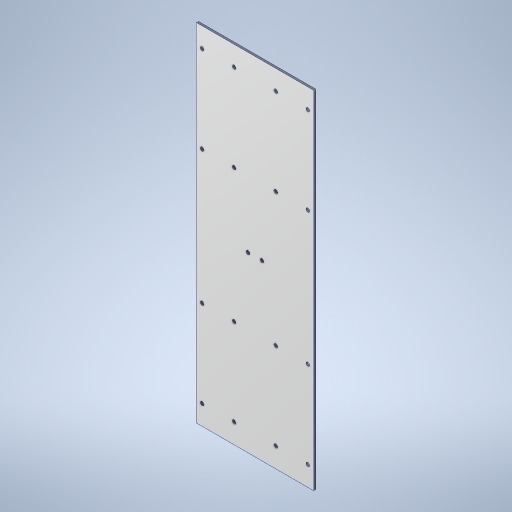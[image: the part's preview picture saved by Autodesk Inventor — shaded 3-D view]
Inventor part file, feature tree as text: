
AUTODESK INVENTOR PART (.ipt)
format: ipt  version: 2024 (Build 280153000, 153)  size: 334,848 bytes
history: native  units: mm
features: sketch x5, extrude x4, hole x3, other x2
ambient origin geometry x8: Origin, YZ Plane, XZ Plane, XY Plane, X Axis, Y Axis, Z Axis, Center Point
bodies: Body1 (feature_tree), Body2 (feature_tree)
feature tree (14):
  other  "Laminate"
  sketch  "Sketch1"  dims[d0=169.5mm d1=499.0mm]
  extrude  "Extrusion1"  Depth=499.0mm
  extrude  "Extrusion2"  Depth=2.9mm TaperAngle=0.0deg
  extrude  "Extrusion3"  Depth=250.0mm
  hole  "Hole2"  [1 undecoded]
  hole  "Hole3"  [1 undecoded]
  hole  "Hole1"  [1 undecoded]
  extrude  "Extrusion4"  TaperAngle=0.0deg  [1 undecoded]
  other  "Core"
  sketch  "Sketch2"  dims[d2=3.0mm d3=0.0mm d4=2.9mm d5=0.0mm]
  sketch  "Sketch3"  dims[d6=2.9mm d7=0.0mm]
  sketch  "Sketch4"  dims[d12=5.4mm d13=6.0mm d14=4.0mm d15=2.0mm d16=90.0deg d17=8.0mm d18=20.594885mm d19=250.0mm]
  sketch  "Sketch5"  dims[d20=120.0mm d22=10.0mm d23=24.0mm d24=3.625mm d25=0.0mm d26=0.0mm d27=1.0mm d28=60.0mm d29=442.0mm d30=125.0mm d31=20.0mm d32=5.4mm d33=6.0mm d34=4.0mm d35=2.0mm d36=90.0deg d37=2.5mm d38=150.0deg d39=152.0mm d40=5.4mm d41=6.0mm d42=4.0mm d43=2.0mm d44=90.0deg d45=8.0mm d46=150.0deg]
note: 4 required parameter values undecoded (feature->parameter linkage not recoverable at this tier; creation-order binding heuristic only, values carry confidence <= 0.55)
